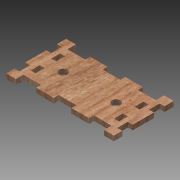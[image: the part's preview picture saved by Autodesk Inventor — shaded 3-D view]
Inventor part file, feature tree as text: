
AUTODESK INVENTOR PART (.ipt)
format: ipt  version: 2015 (Build 190159000, 159)  size: 371,712 bytes
history: native  units: mm
features: other x10, sketch x9, extrude x5, hole x1
ambient origin geometry x8: Origin, YZ Plane, XZ Plane, XY Plane, X Axis, Y Axis, Z Axis, Center Point
bodies: Body1 (feature_tree)
feature tree (25):
  other  "Blocks"
  extrude  "Extrusion2"  Depth=50.0mm
  hole  "Hole5"  [1 undecoded]
  extrude  "Extrusion6"  Depth=20.0mm
  extrude  "Extrusion7"  Depth=5.5mm
  extrude  "Extrusion8"  TaperAngle=0.0deg  [1 undecoded]
  extrude  "Extrusion10"  Depth=10.0mm
  sketch  "Sketch46"  dims[d147=5.5mm]
  sketch  "Sketch47"  dims[d148=0.0mm d155=11.0mm d162=5.5mm d163=0.0mm d164=5.5mm d165=12.0mm d166=12.0mm d172=5.5mm d173=0.0mm d29=1.0mm d30=1.0mm d116=1.0mm d117=1.0mm]
  sketch  "Sketch44"  dims[d146=8.333333mm]
  other  "Kerf0.1"
  sketch  "Sketch10"  dims[d21=100.0mm d22=50.0mm]
  sketch  "Sketch16"  dims[d23=5.5mm d24=0.0mm d52=60.0mm]
  sketch  "Sketch35"  dims[d53=9.5mm d54=6.0mm d55=4.0mm d56=2.0mm d57=90.0deg d58=4.0mm d59=0.0mm d129=20.0mm]
  sketch  "Sketch36"  dims[d130=20.0mm d131=5.5mm]
  sketch  "Sketch37"  dims[d142=5.5mm d143=0.0mm]
  sketch  "Sketch38"  dims[d144=5.5mm d145=10.0mm]
  other  "Block1"
  other  "Block2"
  other  "Block3"
  other  "Block4"
  other  "Block3:1"
  other  "Block3:2"
  other  "Block4:1"
  other  "Block4:2"
note: 2 required parameter values undecoded (feature->parameter linkage not recoverable at this tier; creation-order binding heuristic only, values carry confidence <= 0.55)
